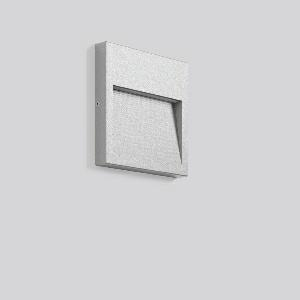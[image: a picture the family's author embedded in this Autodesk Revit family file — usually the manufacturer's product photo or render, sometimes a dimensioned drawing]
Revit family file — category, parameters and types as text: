
# Revit family: brick_midi_581633_004_1_e007
name_source: partatom
category: Lighting Fixtures
units: mm (PartAtom-declared; Revit-internal decimal feet)

## family parameters
Cut with Voids When Loaded = No
Host = Face
Light Source = No
Part Type = Normal
Room Calculation Point = No
Round Connector Dimension = Use Diameter
Shared = No

## types (1)
- BRICK midi (1 x LED Modul 840, 190 lm, 4000)
    Apparent Load = 10 VA
    CIE Flux Codes = 51 81 95 96 100
    Color Rendering = 80
    Color Temperature = 4000
    Default Elevation = 1800 mm
    Description = Series: BRICK midi
Flat surface-mounted LED fitting for illumination of wall related areas such as stairs, ramps or corridors. Housing made of corrosion-resistant die-cast aluminium, powder-coated. Stainless steel screws. Diffuser with clear toughened glass. Asymmetrical downward light distribution for wide dispersion and uniform illumination. With compensation for drill hole deviations. Driver integrated. With connecting terminal up to 1 x 3 x 1.5 mm², for max. 13 mm diameter mains cable. 
Colour: silver, matt (approx. RAL 9006)
Length: 200 mm
Width: 200 mm
Height: 24 mm
Lamp: LED
System power: 10 W
Rated luminous flux: 190 lm
Luminous efficiency: 19 lm/W
Control gear: Regulated power supply
Protection class: I
Type of protection: IP 65
    Height = 24 mm  [stored 0.0787402 ft]
    Lamp = 1 x LED Modul 840
    Lamp Light Flux = 190 lm
    Lamp count = 1
    Length = 200 mm  [stored 0.656168 ft]
    Lifetime = 50000 h
    Luminous efficacy = 19 lm/W
    Manufacturer = RZB
    ModVariant = No
    Model = 581633.004.1
    Mounting Place = Wall
    Mounting Type = Surface mounted
    Number of Poles = 1
    OnlyDefault = Yes
    Power Factor = 1
    Product Name = BRICK midi
    Product group = Surface mounted Wall luminaires
    ProductGroupID = 2001
    Protection Class = Protection class I
    Protection Degree = IP 65
    RLX_Detail_Level = 1
    RLX_Emergency_Light_Flux = 0 lm
    RLX_Emergency_Type = 0
    RLX_Emergency_Type_DB = No
    RlxData = <blob elided: 21997 chars, md5=713314b7>
    Socket = socket
    Standby Power = 0 W
    System Light Flux = 190 lm
    System Power = 10 W
    Type Comments = ALEA SPOT
    Type Image = 581633.004.jpg
    URL = http://relux.com
    VarID = ---
    Voltage = 0 V
    Weight = 0.00 kg
    Width = 200 mm  [stored 0.656168 ft]

note: [stored X ft] marks values corroborated as IEEE doubles in the binary element streams (Revit-internal decimal feet)

## geometry (parser evidence)
native form markers: Blend x4, Sweep x12
no freeform markers — native parametric forms only
